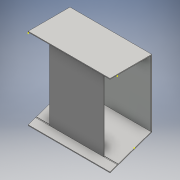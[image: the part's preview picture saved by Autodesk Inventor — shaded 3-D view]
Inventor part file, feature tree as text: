
AUTODESK INVENTOR PART (.ipt)
format: ipt  version: 2016 (Build 200138000, 138)  size: 168,448 bytes
history: native  units: mm
features: sketch x8, extrude x5, other x1
ambient origin geometry x8: Origin, YZ Plane, XZ Plane, XY Plane, X Axis, Y Axis, Z Axis, Center Point
bodies: Body1 (feature_tree)
feature tree (14):
  other  "Bryła1"
  extrude  "Wyciągnięcie proste1"  Depth=88.0mm
  extrude  "Wyciągnięcie proste2"  Depth=54.0mm
  sketch  "Szkic3"
  extrude  "Wyciągnięcie proste3"  Depth=9.0mm
  sketch  "Szkic5"
  sketch  "Szkic6"
  extrude  "Wyciągnięcie proste4"  Depth=1.0mm
  extrude  "Wyciągnięcie proste5"  Depth=54.0mm
  sketch  "Szkic1"
  sketch  "Szkic2"
  sketch  "Szkic4"
  sketch  "Szkic7"
  sketch  "Szkic8"
